# Revit family: is_3360_010478
name_source: partatom
category: Elektroinstallationen
revit_build: Autodesk Revit 2016 (Build: 20190508_0715(x64)
units: mm (PartAtom-declared; Revit-internal decimal feet)

## family parameters
Basisbauteil = Fläche
Beim Laden mit Abzugskörper schneiden = Nein
Bemaßung runder Anschluss = Durchmesser verwenden
Beschriftungsausrichtung beibehalten = Nein
Gemeinsam genutzt = Nein
Raumberechnungspunkt = Nein
Teiletyp = Normal

## types (1)
- IS 3360
    Apparent Load = 0 VA
    Beschreibung = Type: Motion detectors; Dimensions (L x W x H): 65 x 95 x 95 mm; Mains power supply: 220 – 240 V / 50 – 60 Hz; Sensor Technology: passive infrared; Application, place: Outdoors, Indoors; Application, room: production facilities, recreation room, changing room, function room / ancillary room, sports hall, reception / lobby, stairwell, WC / washroom, multi-storey / underground car park, outdoors, warehouse, Indoors; Installation site: ceiling; Installation: Surface wiring; Switching zones: 1416 switching zones; Electronic scalability: No; Mechanical scalability: No; Mounting height: 2,50 – 4,00 m; Optimum mounting height: 2,8 m; Detection angle: 360 °; Angle of aperture: 180 °; Sneak-by guard: Yes; Capability of masking out individual segments: Yes; Reach, radial: Ø 8 m (50 m²); Reach, tangential: Ø 40 m (1257 m²); Reach, presence: Ø 3 m (7 m²); Twilight setting TEACH: Yes; Twilight setting: 2 – 1000 lx; Time setting: 5 sec – 15 min; Switching output 1, resistive: 2000 W; Switching output 1, number of LEDs / fluorescent lamps: 8 pcs.; Constant-lighting control: No; Basic light level function: No; Functions: Normal / test mode, Manual ON / ON-OFF; Settings via: Remote control, Potentiometers, Smart Remote; With remote control: No; Interconnection: Yes; IP-rating: IP54; Material: Plastic; Ambient temperature: -20 – 50 °C; Colour: white; Colour, RAL: 9003; Manufacturer's Warranty: 5 years; Version: COM1 - surface, sq. white; PU1, EAN: 4007841010478
    Height = 95 mm
    Hersteller = Steinel
    Length = 65 mm
    Maximum range = 20.158 m
    ModVariant = Nein
    Modell = 010478
    Mounting Place = Ceiling
    Mounting Type = Surface mounted
    Number of Poles = 1
    OnlyDefault = Ja
    Power Factor = 1
    Product Name = IS 3360
    Product group = Sensor-switched outdoor light
    ProductGroupID = 3
    Protection Class = Protection class
    Protection Degree = IP 54
    RlxData = <blob elided: 185157 chars, md5=5b2b8905>
    Sensor characteristics = Circular 300°-360°
    Sensor type = Passive (infrared)
    SensorDataFile = <blob elided: 6785 chars, md5=23016e95>
    Type of entry = Presence, Motion
    Typenbild = produkt1_010478.jpg
    Typenkommentare = Product without accessories
    URL = http://relux.com
    VarID = ---
    Voltage = 0 V
    Vorgabe-Ansicht = 1800 mm
    Weight = 0.00 kg
    Width = 95 mm

## geometry (parser evidence)
native form markers: Blend x4, Sweep x21
no freeform markers — native parametric forms only
